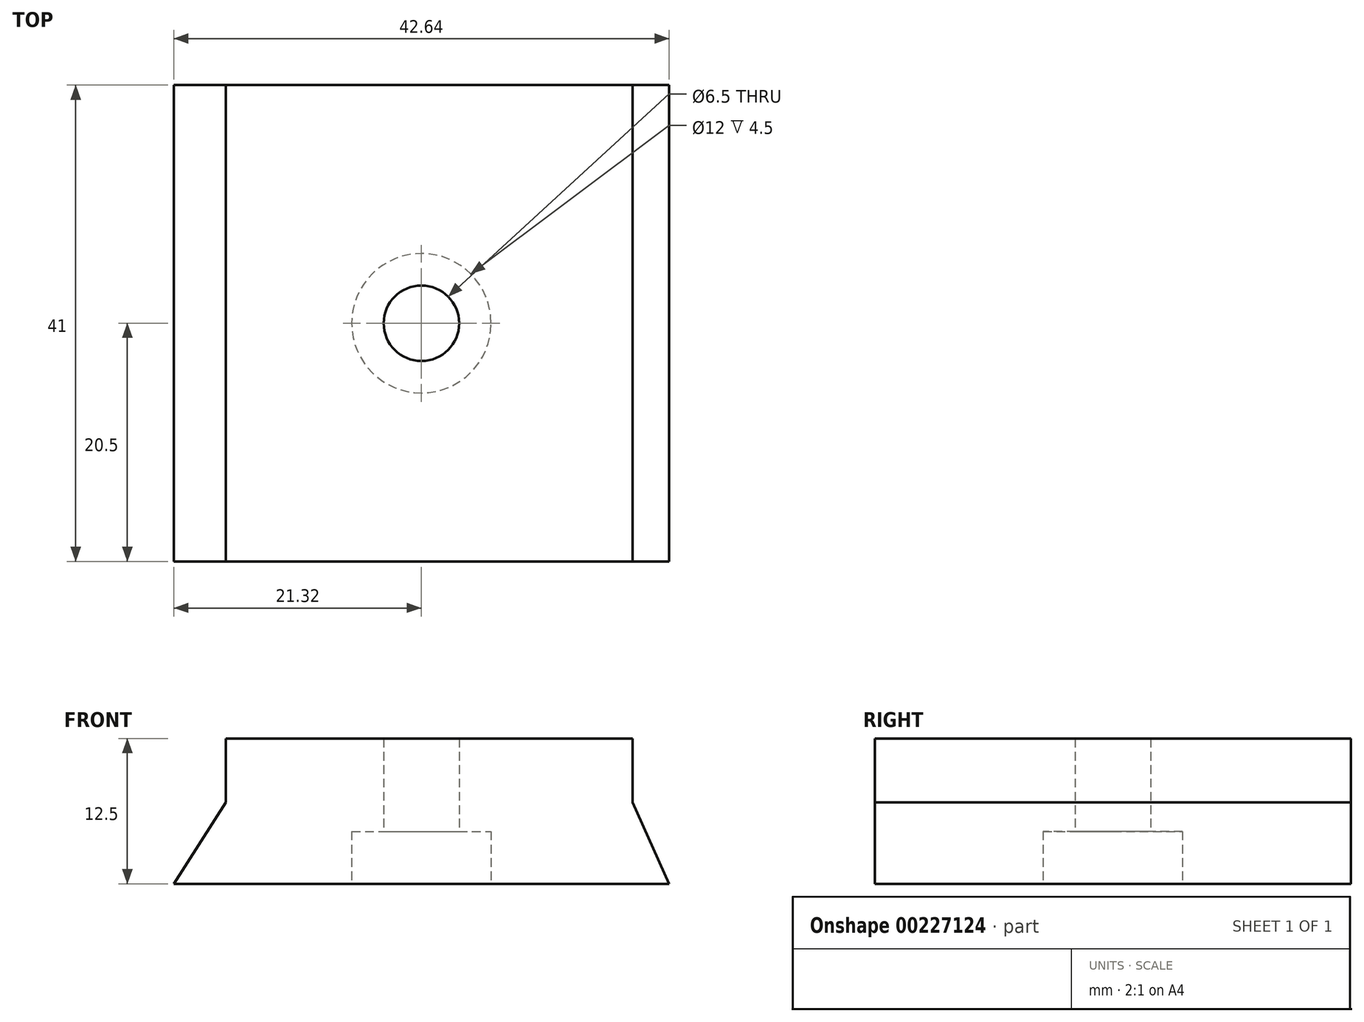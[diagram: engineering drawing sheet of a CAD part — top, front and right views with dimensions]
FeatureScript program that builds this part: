
annotation { "Feature Type Name" : "Feature", "Feature Type Description" : "" }
export const myFeature = defineFeature(function(context is Context, id is Id, definition is map)
    precondition{}
    {
        {
            var Q0;
            Q0=qCreatedBy(makeId("Front.planeOp"),FACE);
            var sketch = newSketch(context, id + "F0", { "sketchPlane" : qUnion([Q0])});
            skLineSegment(sketch, "E0", {"start": v(-21.33, 0) * mm, "end": v(21.33, 0) * mm});
            skLineSegment(sketch, "E1", {"start": v(21.32, 0) * mm, "end": v(18.18, 7) * mm});
            skLineSegment(sketch, "E2", {"start": v(18.18, 7) * mm, "end": v(-16.82, 7) * mm});
            skLineSegment(sketch, "E3", {"start": v(-16.82, 7) * mm, "end": v(-21.32, 0) * mm});
            skSolve(sketch);
        }
        {
            var Q0;
            Q0=makeQuery(id+"F0.imprint","IMPRINT",FACE,{"disambiguationData":[TD([[makeQuery(id+"F0.imprint","IMPRINT",EDGE,{"derivedFrom":sQuery(id+"F0.wireOp",EDGE,"E0")}),1.0]])]});
            extrude(context, id + "F1", {"entities" : qUnion([Q0]), "endBound" : BoundingType.SYMMETRIC, "depth" : 41 * mm});
        }
        {
            var Q0;
            Q0=makeQuery(id+"F1.opExtrude","SWEPT_FACE",FACE,{"disambiguationData":[OSD([sQuery(id+"F0.wireOp",EDGE,"E0")])]});
            var sketch = newSketch(context, id + "F2", { "sketchPlane" : qUnion([Q0])});
            skPoint(sketch, "E4", {"position": v(0, 0) * mm});
            skSolve(sketch);
        }
        {
            var Q0;
            Q0=sQuery(id+"F2.wireOp",VERTEX,"E4");
            var Q1;
            Q1=makeQuery(id+"F1.opExtrude","SWEPT_BODY",BODY,{"disambiguationData":[OSD([sQuery(id+"F0.wireOp",EDGE,"E0"),sQuery(id+"F0.wireOp",EDGE,"E1"),sQuery(id+"F0.wireOp",EDGE,"E2"),sQuery(id+"F0.wireOp",EDGE,"E3")])]});
            hole(context, id + "F3", {"style" : HoleStyle.C_BORE, "endStyle" : HoleEndStyle.THROUGH, "holeDiameter" : 6.5 * mm, "cBoreDiameter" : 12 * mm, "cBoreDepth" : 4.5 * mm, "locations" : qUnion([Q0]), "scope" : qUnion([Q1]), "isTappedThrough" : true});
        }
        {
            var Q0;
            Q0=makeQuery(id+"F1.opExtrude","SWEPT_FACE",FACE,{"disambiguationData":[OSD([sQuery(id+"F0.wireOp",EDGE,"E2")])]});
            extrude(context, id + "F4", {"entities" : qUnion([Q0]), "operationType" : NewBodyOperationType.ADD, "depth" : (8 - 2.5) * mm});
        }
    });
